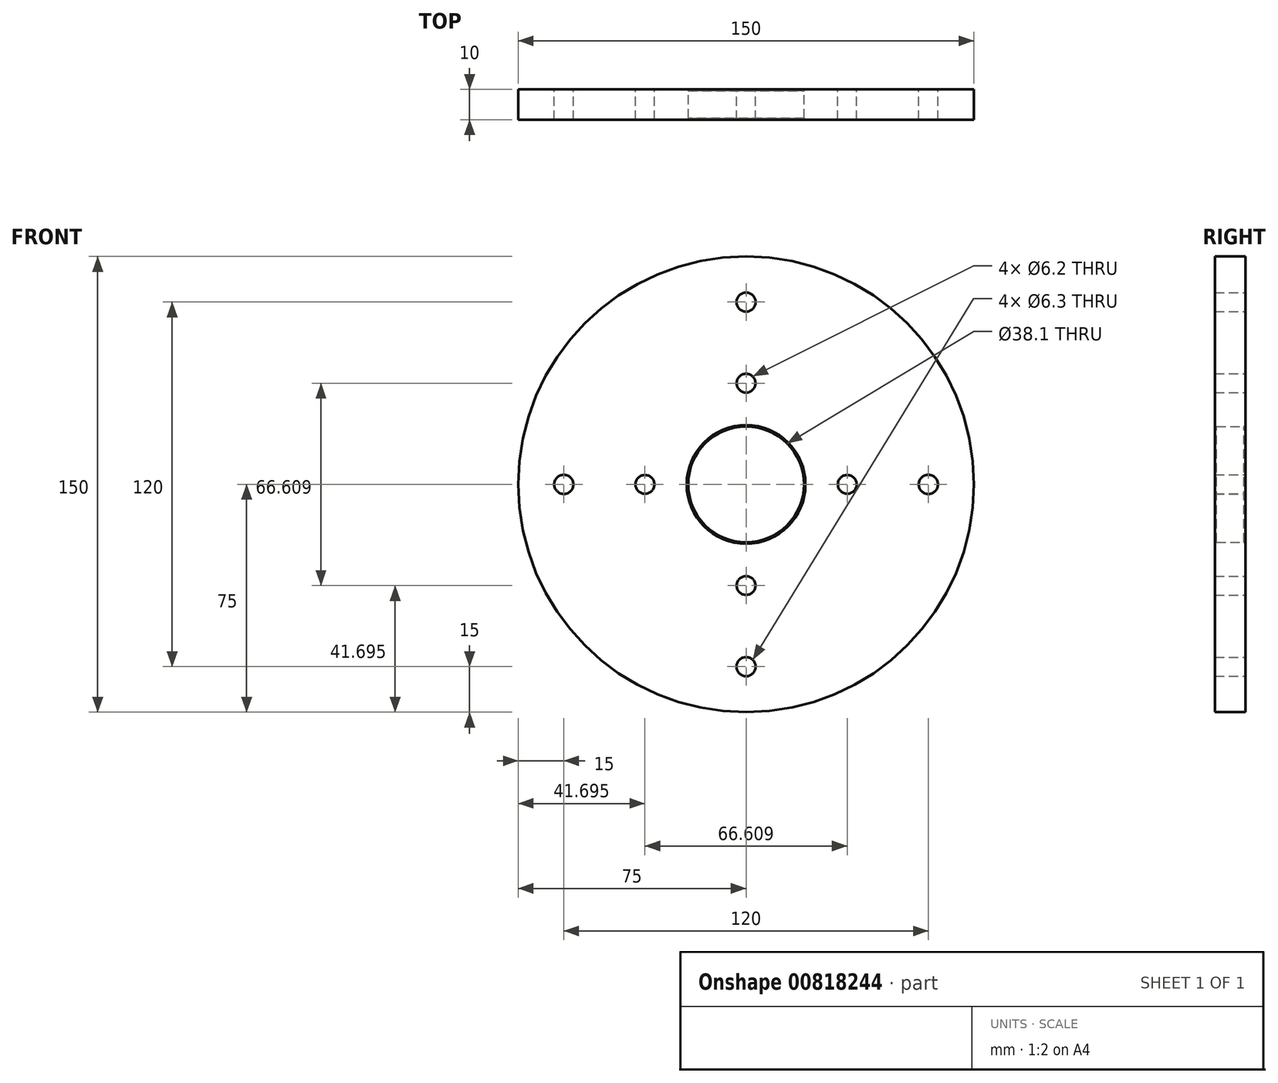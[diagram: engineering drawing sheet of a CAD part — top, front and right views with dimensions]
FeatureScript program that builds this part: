
annotation { "Feature Type Name" : "Feature", "Feature Type Description" : "" }
export const myFeature = defineFeature(function(context is Context, id is Id, definition is map)
    precondition{}
    {
        {
            var Q0;
            Q0=qCreatedBy(makeId("Front.planeOp"),FACE);
            var sketch = newSketch(context, id + "F0", { "sketchPlane" : qUnion([Q0])});
            skCircle(sketch, "E0", {"center": v(0, 0) * mm, "radius": 75 * mm});
            skCircle(sketch, "E1", {"center": v(0, 0) * mm, "radius": 19.05 * mm});
            skSolve(sketch);
        }
        {
            var Q0;
            Q0=qSketchRegion(id+"F0",true);
            extrude(context, id + "F1", {"entities" : qUnion([Q0]), "depth" : 10 * mm, "offsetDistance" : 25 * mm});
        }
        {
            var Q0;
            Q0=makeQuery(id+"F0.imprint","IMPRINT",FACE,{"disambiguationData":[TD([[makeQuery(id+"F0.imprint","IMPRINT",EDGE,{"derivedFrom":sQuery(id+"F0.wireOp",EDGE,"E0")}),1.0]])]});
            var sketch = newSketch(context, id + "F2", { "sketchPlane" : qUnion([Q0])});
            skCircle(sketch, "E2", {"center": v(0, 33.3) * mm, "radius": 3.1 * mm});
            skCircle(sketch, "E3", {"center": v(33.3, 0) * mm, "radius": 3.1 * mm});
            skCircle(sketch, "E4", {"center": v(0, -33.3) * mm, "radius": 3.1 * mm});
            skCircle(sketch, "E5", {"center": v(-33.3, 0) * mm, "radius": 3.1 * mm});
            skLineSegment(sketch, "E6.bottom", {"start": v(23.55, -23.55) * mm, "end": v(-23.55, -23.55) * mm, "construction": true});
            skLineSegment(sketch, "E6.top", {"start": v(23.55, 23.55) * mm, "end": v(-23.55, 23.55) * mm, "construction": true});
            skLineSegment(sketch, "E6.left", {"start": v(23.55, -23.55) * mm, "end": v(23.55, 23.55) * mm, "construction": true});
            skLineSegment(sketch, "E6.right", {"start": v(-23.55, -23.55) * mm, "end": v(-23.55, 23.55) * mm, "construction": true});
            skCircle(sketch, "E7", {"center": v(0, 0) * mm, "radius": 33.3 * mm, "construction": true});
            skSolve(sketch);
        }
        {
            var Q0;
            Q0=qSketchRegion(id+"F2",true);
            var Q1;
            Q1=makeQuery(id+"F1.opExtrude","CAP_FACE",FACE,{"disambiguationData":[OSD([sQuery(id+"F0.wireOp",EDGE,"E0"),sQuery(id+"F0.wireOp",EDGE,"E1")])],"isStart":false});
            extrude(context, id + "F3", {"entities" : qUnion([Q0]), "operationType" : NewBodyOperationType.REMOVE, "endBound" : BoundingType.UP_TO_SURFACE, "depth" : 25 * mm, "endBoundEntityFace" : qUnion([Q1]), "offsetDistance" : 25 * mm});
        }
        {
            var Q0;
            Q0=makeQuery(id+"F3.boolean.opBoolean","COPY",EDGE,{"derivedFrom":makeQuery(id+"F3.opExtrude","TWEAK_EDGE",EDGE,{"derivedFrom":[makeQuery(id+"F1.opExtrude","CAP_FACE",FACE,{"disambiguationData":[OSD([sQuery(id+"F0.wireOp",EDGE,"E0"),sQuery(id+"F0.wireOp",EDGE,"E1")])],"isStart":false}),makeQuery(id+"F2.imprint","IMPRINT",EDGE,{"derivedFrom":sQuery(id+"F2.wireOp",EDGE,"E5")})]})});
            var Q1;
            Q1=makeQuery(id+"F3.boolean.opBoolean","COPY",EDGE,{"derivedFrom":makeQuery(id+"F3.opExtrude","TWEAK_EDGE",EDGE,{"derivedFrom":[makeQuery(id+"F1.opExtrude","CAP_FACE",FACE,{"disambiguationData":[OSD([sQuery(id+"F0.wireOp",EDGE,"E0"),sQuery(id+"F0.wireOp",EDGE,"E1")])],"isStart":false}),makeQuery(id+"F2.imprint","IMPRINT",EDGE,{"derivedFrom":sQuery(id+"F2.wireOp",EDGE,"E2")})]})});
            var Q2;
            Q2=makeQuery(id+"F3.boolean.opBoolean","COPY",EDGE,{"derivedFrom":makeQuery(id+"F3.opExtrude","TWEAK_EDGE",EDGE,{"derivedFrom":[makeQuery(id+"F1.opExtrude","CAP_FACE",FACE,{"disambiguationData":[OSD([sQuery(id+"F0.wireOp",EDGE,"E0"),sQuery(id+"F0.wireOp",EDGE,"E1")])],"isStart":false}),makeQuery(id+"F2.imprint","IMPRINT",EDGE,{"derivedFrom":sQuery(id+"F2.wireOp",EDGE,"E3")})]})});
            var Q3;
            Q3=makeQuery(id+"F3.boolean.opBoolean","COPY",EDGE,{"derivedFrom":makeQuery(id+"F3.opExtrude","TWEAK_EDGE",EDGE,{"derivedFrom":[makeQuery(id+"F1.opExtrude","CAP_FACE",FACE,{"disambiguationData":[OSD([sQuery(id+"F0.wireOp",EDGE,"E0"),sQuery(id+"F0.wireOp",EDGE,"E1")])],"isStart":false}),makeQuery(id+"F2.imprint","IMPRINT",EDGE,{"derivedFrom":sQuery(id+"F2.wireOp",EDGE,"E4")})]})});
            var Q4;
            Q4=makeQuery(id+"F3.boolean.opBoolean","COPY",EDGE,{"derivedFrom":makeQuery(id+"F3.opExtrude","CAP_EDGE",EDGE,{"disambiguationData":[OSD([sQuery(id+"F2.wireOp",EDGE,"E4")])],"isStart":true})});
            var Q5;
            Q5=makeQuery(id+"F3.boolean.opBoolean","COPY",EDGE,{"derivedFrom":makeQuery(id+"F3.opExtrude","CAP_EDGE",EDGE,{"disambiguationData":[OSD([sQuery(id+"F2.wireOp",EDGE,"E5")])],"isStart":true})});
            var Q6;
            Q6=makeQuery(id+"F3.boolean.opBoolean","COPY",EDGE,{"derivedFrom":makeQuery(id+"F3.opExtrude","CAP_EDGE",EDGE,{"disambiguationData":[OSD([sQuery(id+"F2.wireOp",EDGE,"E2")])],"isStart":true})});
            var Q7;
            Q7=makeQuery(id+"F3.boolean.opBoolean","COPY",EDGE,{"derivedFrom":makeQuery(id+"F3.opExtrude","CAP_EDGE",EDGE,{"disambiguationData":[OSD([sQuery(id+"F2.wireOp",EDGE,"E3")])],"isStart":true})});
            var Q8;
            Q8=makeQuery(id+"F1.opExtrude","CAP_EDGE",EDGE,{"disambiguationData":[OSD([sQuery(id+"F0.wireOp",EDGE,"E1")])],"isStart":true});
            var Q9;
            Q9=makeQuery(id+"F1.opExtrude","CAP_EDGE",EDGE,{"disambiguationData":[OSD([sQuery(id+"F0.wireOp",EDGE,"E1")])],"isStart":false});
            chamfer(context, id + "F4", {"entities" : qUnion([Q0, Q1, Q2, Q3, Q4, Q5, Q6, Q7, Q8, Q9]), "width" : 0.5 * mm, "tangentPropagation" : true});
        }
        {
            var Q0;
            Q0=makeQuery(id+"F0.imprint","IMPRINT",FACE,{"disambiguationData":[TD([[makeQuery(id+"F0.imprint","IMPRINT",EDGE,{"derivedFrom":sQuery(id+"F0.wireOp",EDGE,"E0")}),1.0]])]});
            var sketch = newSketch(context, id + "F5", { "sketchPlane" : qUnion([Q0])});
            skCircle(sketch, "E8", {"center": v(0, 0) * mm, "radius": 60 * mm, "construction": true});
            skCircle(sketch, "E9", {"center": v(60, 0) * mm, "radius": 3.15 * mm});
            skCircle(sketch, "E10.1.0", {"center": v(0, 60) * mm, "radius": 3.15 * mm});
            skCircle(sketch, "E10.2.0", {"center": v(-60, 0) * mm, "radius": 3.15 * mm});
            skCircle(sketch, "E10.3.0", {"center": v(0, -60) * mm, "radius": 3.15 * mm});
            skSolve(sketch);
        }
        {
            var Q0;
            Q0 = qSketchRegion(id + "F5", true);
            extrude(context, id + "F6", {"entities" : qUnion([Q0]), "operationType" : NewBodyOperationType.REMOVE, "depth" : 25 * mm, "offsetDistance" : 25 * mm});
        }
    });
